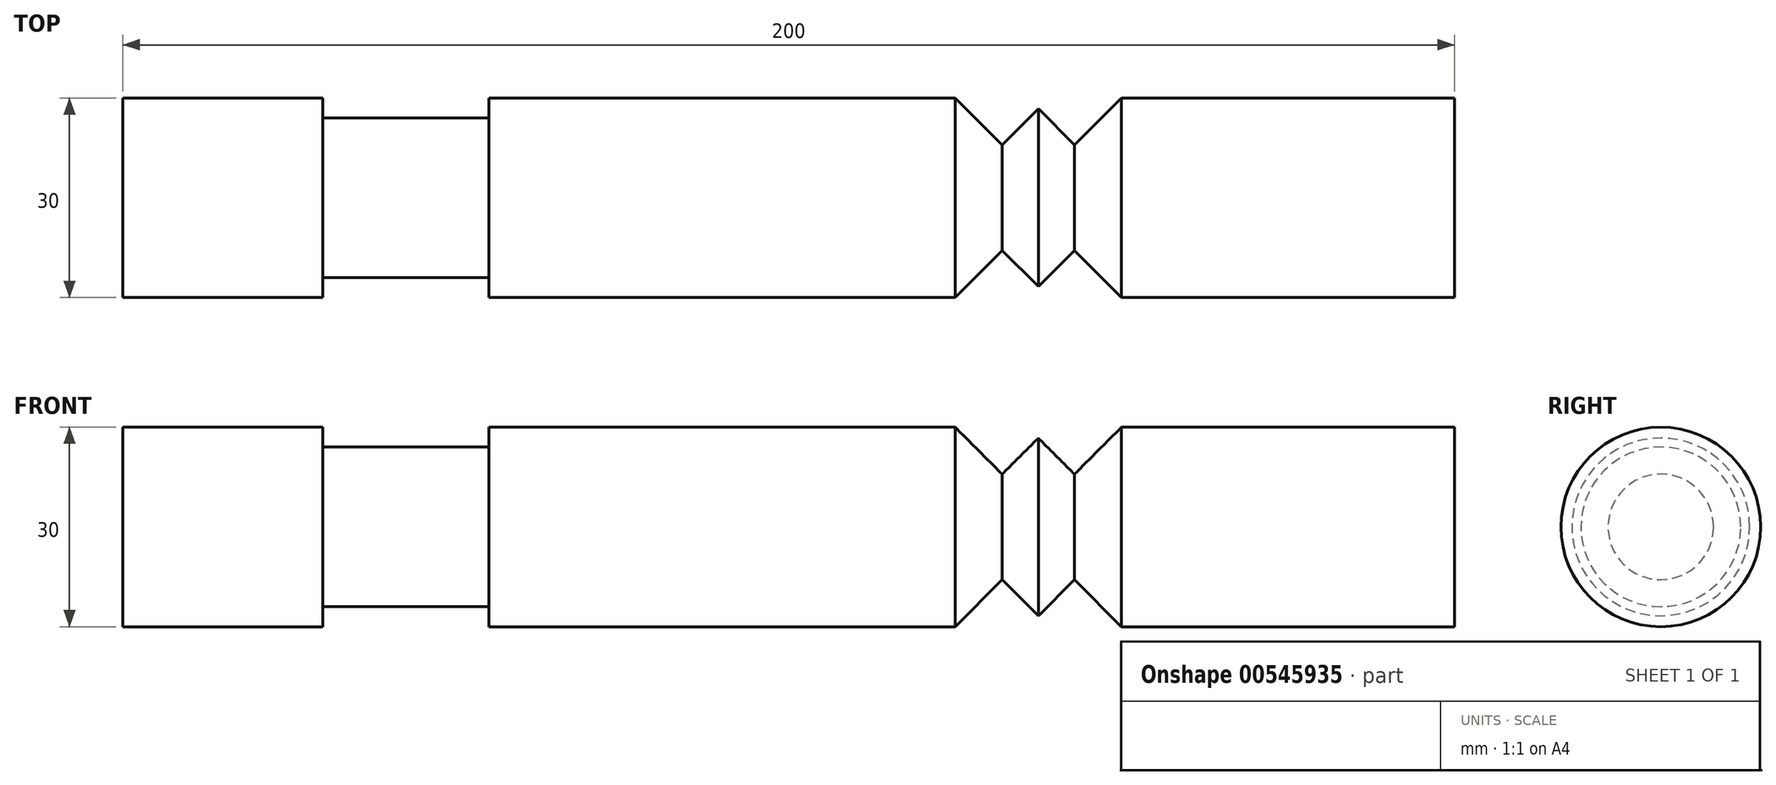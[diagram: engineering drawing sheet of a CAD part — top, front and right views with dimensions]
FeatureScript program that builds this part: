
annotation { "Feature Type Name" : "Feature", "Feature Type Description" : "" }
export const myFeature = defineFeature(function(context is Context, id is Id, definition is map)
    precondition{}
    {
        {
            var Q0;
            Q0=qCreatedBy(makeId("Front.planeOp"),FACE);
            var sketch = newSketch(context, id + "F0", { "sketchPlane" : qUnion([Q0])});
            skLineSegment(sketch, "E0.bottom", {"start": v(0, 0) * mm, "end": v(200, 0) * mm});
            skLineSegment(sketch, "E0.top", {"start": v(0, 15) * mm, "end": v(30, 15) * mm});
            skLineSegment(sketch, "E0.left", {"start": v(0, 0) * mm, "end": v(0, 15) * mm});
            skLineSegment(sketch, "E0.right", {"start": v(200, 0) * mm, "end": v(200, 15) * mm});
            skLineSegment(sketch, "E1.top", {"start": v(30, 12) * mm, "end": v(55, 12) * mm});
            skLineSegment(sketch, "E1.left", {"start": v(30, 15) * mm, "end": v(30, 12) * mm});
            skLineSegment(sketch, "E1.right", {"start": v(55, 15) * mm, "end": v(55, 12) * mm});
            skLineSegment(sketch, "E2.trimOffspring", {"start": v(55, 15) * mm, "end": v(125, 15) * mm});
            skLineSegment(sketch, "E3", {"start": v(-33.9, 0) * mm, "end": v(233.72, 0) * mm, "construction": true});
            skPoint(sketch, "E3.endSnap0", {"position": v(100, 0) * mm});
            skLineSegment(sketch, "E4", {"start": v(125, 15) * mm, "end": v(132.07, 7.93) * mm});
            skLineSegment(sketch, "E5", {"start": v(132.07, 7.93) * mm, "end": v(137.5, 13.36) * mm});
            skLineSegment(sketch, "E6", {"start": v(137.5, 13.36) * mm, "end": v(142.93, 7.93) * mm});
            skLineSegment(sketch, "E7", {"start": v(142.93, 7.93) * mm, "end": v(150, 15) * mm});
            skLineSegment(sketch, "E8.trimOffspring", {"start": v(150, 15) * mm, "end": v(200, 15) * mm});
            skSolve(sketch);
        }
        {
            var Q0;
            Q0=makeQuery(id+"F0.imprint","IMPRINT",FACE,{"disambiguationData":[TD([[makeQuery(id+"F0.imprint","IMPRINT",EDGE,{"derivedFrom":sQuery(id+"F0.wireOp",EDGE,"E0.bottom")}),1.0]])]});
            var Q1;
            Q1=sQuery(id+"F0.wireOp",EDGE,"E3");
            revolve(context, id + "F1", {"entities" : qUnion([Q0]), "axis" : qUnion([Q1]), "revolveType" : RevolveType.FULL});
        }
    });
